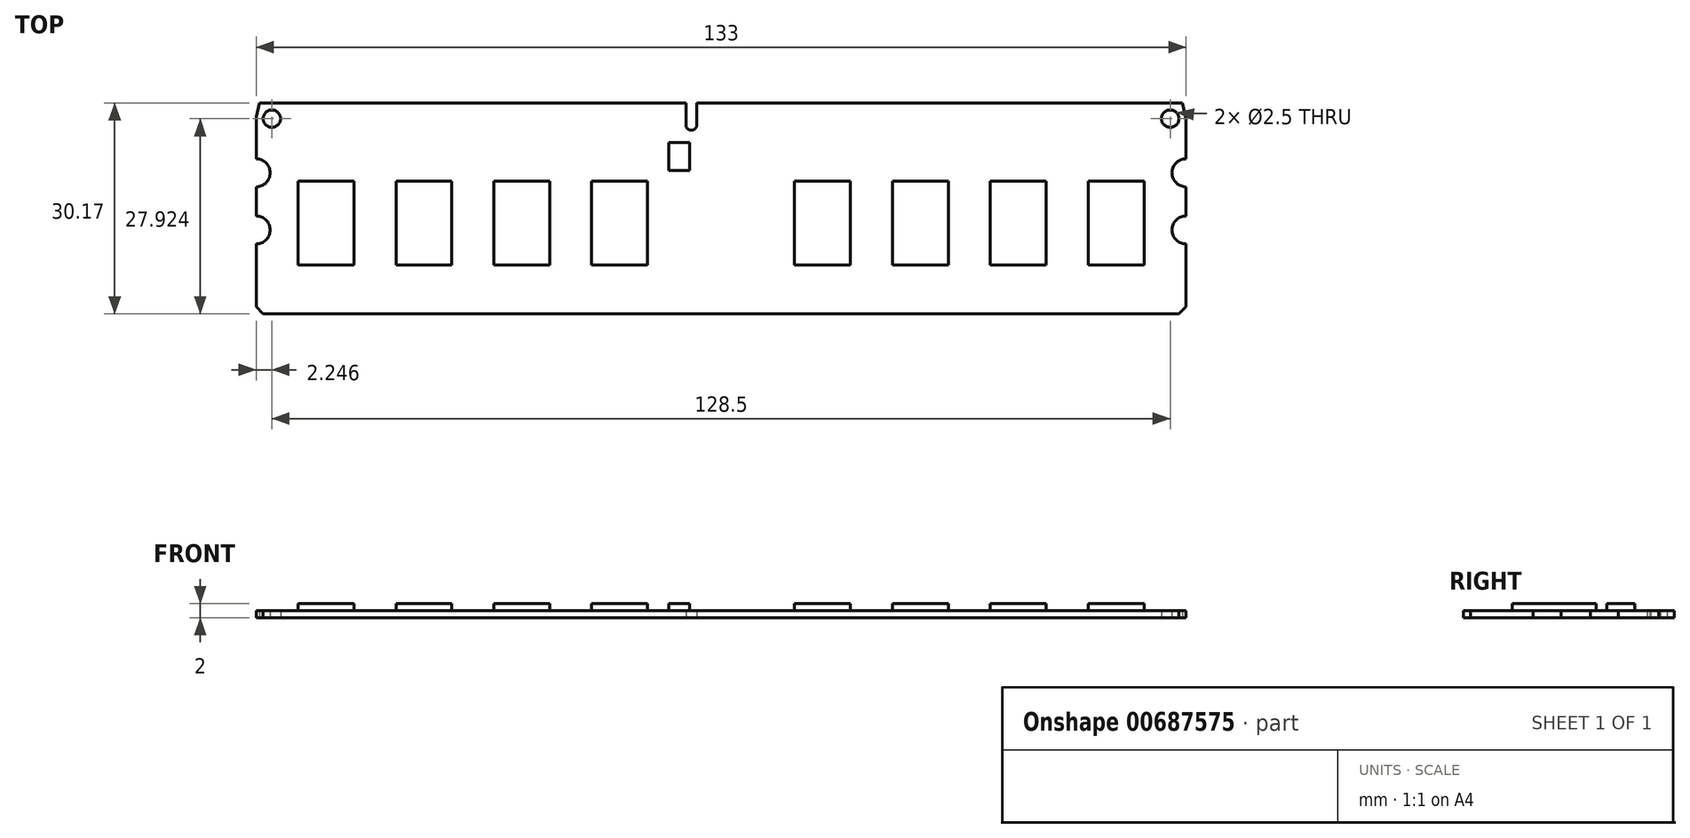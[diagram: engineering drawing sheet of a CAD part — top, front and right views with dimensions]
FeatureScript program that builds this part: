
annotation { "Feature Type Name" : "Feature", "Feature Type Description" : "" }
export const myFeature = defineFeature(function(context is Context, id is Id, definition is map)
    precondition{}
    {
        {
            var Q0;
            Q0=qCreatedBy(makeId("Top.planeOp"),FACE);
            var sketch = newSketch(context, id + "F0", { "sketchPlane" : qUnion([Q0])});
            skLineSegment(sketch, "E0.bottom", {"start": v(-59.6, 3.36) * mm, "end": v(1.4, 3.36) * mm});
            skLineSegment(sketch, "E0.top", {"start": v(-59.1, -26.81) * mm, "end": v(71.9, -26.81) * mm});
            skLineSegment(sketch, "E0.left", {"start": v(-60.1, 1.36) * mm, "end": v(-60.1, -4.64) * mm});
            skLineSegment(sketch, "E0.right", {"start": v(72.9, 1.13) * mm, "end": v(72.9, -4.64) * mm});
            skPoint(sketch, "E1.center.orphan", {"position": v(-60.1, -16.81) * mm});
            skArc(sketch, "E2", {"start": v(-60.1, -16.81) * mm, "mid": v(-58.1, -14.81) * mm, "end": v(-60.1, -12.81) * mm});
            skArc(sketch, "E3", {"start": v(-60.1, -8.64) * mm, "mid": v(-58.1, -6.64) * mm, "end": v(-60.1, -4.64) * mm});
            skLineSegment(sketch, "E4.trimOffspring", {"start": v(-60.1, -8.64) * mm, "end": v(-60.1, -12.81) * mm});
            skLineSegment(sketch, "E5.trimOffspring", {"start": v(-60.1, -16.81) * mm, "end": v(-60.1, -25.81) * mm});
            skArc(sketch, "E6", {"start": v(72.9, -4.64) * mm, "mid": v(70.9, -6.64) * mm, "end": v(72.9, -8.64) * mm});
            skArc(sketch, "E7", {"start": v(72.9, -12.81) * mm, "mid": v(70.9, -14.81) * mm, "end": v(72.9, -16.81) * mm});
            skLineSegment(sketch, "E8.trimOffspring", {"start": v(72.9, -8.64) * mm, "end": v(72.9, -12.81) * mm});
            skLineSegment(sketch, "E9.trimOffspring", {"start": v(72.9, -16.81) * mm, "end": v(72.9, -25.81) * mm});
            skLineSegment(sketch, "E10", {"start": v(-60.1, 1.36) * mm, "end": v(-59.6, 3.36) * mm});
            skLineSegment(sketch, "E11", {"start": v(72.9, 1.13) * mm, "end": v(72.4, 3.36) * mm});
            skLineSegment(sketch, "E12", {"start": v(-60.1, -25.81) * mm, "end": v(-59.1, -26.81) * mm});
            skLineSegment(sketch, "E13", {"start": v(72.9, -25.81) * mm, "end": v(71.9, -26.81) * mm});
            skLineSegment(sketch, "E14", {"start": v(72.4, 13.73) * mm, "end": v(2.9, 13.73) * mm});
            skLineSegment(sketch, "E15", {"start": v(-60.1, 13.73) * mm, "end": v(1.4, 13.73) * mm});
            skLineSegment(sketch, "E16", {"start": v(1.4, 3.36) * mm, "end": v(1.4, 0) * mm});
            skLineSegment(sketch, "E17", {"start": v(2.9, 3.36) * mm, "end": v(2.9, 0) * mm});
            skArc(sketch, "E18", {"start": v(1.4, 0) * mm, "mid": v(2.16, -0.55) * mm, "end": v(2.9, 0) * mm});
            skLineSegment(sketch, "E19.trimOffspring", {"start": v(2.9, 3.36) * mm, "end": v(72.4, 3.36) * mm});
            skCircle(sketch, "E20", {"center": v(-57.84, 1.11) * mm, "radius": 1.25 * mm});
            skCircle(sketch, "E21", {"center": v(70.66, 1.11) * mm, "radius": 1.25 * mm});
            skSolve(sketch);
        }
        {
            var Q0;
            Q0=makeQuery(id+"F0.imprint","IMPRINT",FACE,{"disambiguationData":[TD([[makeQuery(id+"F0.imprint","IMPRINT",EDGE,{"derivedFrom":sQuery(id+"F0.wireOp",EDGE,"E0.bottom")}),-1.0]])]});
            extrude(context, id + "F1", {"entities" : qUnion([Q0]), "depth" : 1 * mm, "offsetDistance" : 25 * mm});
        }
        {
            var Q0;
            Q0=makeQuery(id+"F1.opExtrude","CAP_FACE",FACE,{"disambiguationData":[OSD([sQuery(id+"F0.wireOp",EDGE,"E0.bottom"),sQuery(id+"F0.wireOp",EDGE,"E0.top"),sQuery(id+"F0.wireOp",EDGE,"E0.left"),sQuery(id+"F0.wireOp",EDGE,"E0.right"),sQuery(id+"F0.wireOp",EDGE,"E2"),sQuery(id+"F0.wireOp",EDGE,"E3"),sQuery(id+"F0.wireOp",EDGE,"E4.trimOffspring"),sQuery(id+"F0.wireOp",EDGE,"E5.trimOffspring"),sQuery(id+"F0.wireOp",EDGE,"E6"),sQuery(id+"F0.wireOp",EDGE,"E7"),sQuery(id+"F0.wireOp",EDGE,"E8.trimOffspring"),sQuery(id+"F0.wireOp",EDGE,"E9.trimOffspring"),sQuery(id+"F0.wireOp",EDGE,"E10"),sQuery(id+"F0.wireOp",EDGE,"E11"),sQuery(id+"F0.wireOp",EDGE,"E12"),sQuery(id+"F0.wireOp",EDGE,"E13"),sQuery(id+"F0.wireOp",EDGE,"E16"),sQuery(id+"F0.wireOp",EDGE,"E17"),sQuery(id+"F0.wireOp",EDGE,"E18"),sQuery(id+"F0.wireOp",EDGE,"E19.trimOffspring"),sQuery(id+"F0.wireOp",EDGE,"E20"),sQuery(id+"F0.wireOp",EDGE,"E21")])],"isStart":false});
            var sketch = newSketch(context, id + "F2", { "sketchPlane" : qUnion([Q0])});
            skLineSegment(sketch, "E22.bottom", {"start": v(-54.1, -19.81) * mm, "end": v(-46.1, -19.81) * mm});
            skLineSegment(sketch, "E22.top", {"start": v(-54.1, -7.81) * mm, "end": v(-46.1, -7.81) * mm});
            skLineSegment(sketch, "E22.left", {"start": v(-54.1, -19.81) * mm, "end": v(-54.1, -7.81) * mm});
            skLineSegment(sketch, "E22.right", {"start": v(-46.1, -19.81) * mm, "end": v(-46.1, -7.81) * mm});
            skLineSegment(sketch, "E23.bottom", {"start": v(-40.1, -19.81) * mm, "end": v(-32.1, -19.81) * mm});
            skLineSegment(sketch, "E23.top", {"start": v(-40.1, -7.81) * mm, "end": v(-32.1, -7.81) * mm});
            skLineSegment(sketch, "E23.left", {"start": v(-40.1, -19.81) * mm, "end": v(-40.1, -7.81) * mm});
            skLineSegment(sketch, "E23.right", {"start": v(-32.1, -19.81) * mm, "end": v(-32.1, -7.81) * mm});
            skLineSegment(sketch, "E24.bottom", {"start": v(-26.1, -7.81) * mm, "end": v(-18.1, -7.81) * mm});
            skLineSegment(sketch, "E24.top", {"start": v(-26.1, -19.81) * mm, "end": v(-18.1, -19.81) * mm});
            skLineSegment(sketch, "E24.left", {"start": v(-26.1, -7.81) * mm, "end": v(-26.1, -19.81) * mm});
            skLineSegment(sketch, "E24.right", {"start": v(-18.1, -7.81) * mm, "end": v(-18.1, -19.81) * mm});
            skLineSegment(sketch, "E25.bottom", {"start": v(-12.1, -7.81) * mm, "end": v(-4.1, -7.81) * mm});
            skLineSegment(sketch, "E25.top", {"start": v(-12.1, -19.81) * mm, "end": v(-4.1, -19.81) * mm});
            skLineSegment(sketch, "E25.left", {"start": v(-12.1, -7.81) * mm, "end": v(-12.1, -19.81) * mm});
            skLineSegment(sketch, "E25.right", {"start": v(-4.1, -7.81) * mm, "end": v(-4.1, -19.81) * mm});
            skLineSegment(sketch, "E26.bottom", {"start": v(66.9, -7.81) * mm, "end": v(58.9, -7.81) * mm});
            skLineSegment(sketch, "E26.top", {"start": v(66.9, -19.81) * mm, "end": v(58.9, -19.81) * mm});
            skLineSegment(sketch, "E26.left", {"start": v(66.9, -7.81) * mm, "end": v(66.9, -19.81) * mm});
            skLineSegment(sketch, "E26.right", {"start": v(58.9, -7.81) * mm, "end": v(58.9, -19.81) * mm});
            skLineSegment(sketch, "E27.bottom", {"start": v(52.9, -7.81) * mm, "end": v(44.9, -7.81) * mm});
            skLineSegment(sketch, "E27.top", {"start": v(52.9, -19.81) * mm, "end": v(44.9, -19.81) * mm});
            skLineSegment(sketch, "E27.left", {"start": v(52.9, -7.81) * mm, "end": v(52.9, -19.81) * mm});
            skLineSegment(sketch, "E27.right", {"start": v(44.9, -7.81) * mm, "end": v(44.9, -19.81) * mm});
            skLineSegment(sketch, "E28.bottom", {"start": v(38.9, -7.81) * mm, "end": v(30.9, -7.81) * mm});
            skLineSegment(sketch, "E28.top", {"start": v(38.9, -19.81) * mm, "end": v(30.9, -19.81) * mm});
            skLineSegment(sketch, "E28.left", {"start": v(38.9, -7.81) * mm, "end": v(38.9, -19.81) * mm});
            skLineSegment(sketch, "E28.right", {"start": v(30.9, -7.81) * mm, "end": v(30.9, -19.81) * mm});
            skLineSegment(sketch, "E29.bottom", {"start": v(24.9, -7.81) * mm, "end": v(16.9, -7.81) * mm});
            skLineSegment(sketch, "E29.top", {"start": v(24.9, -19.81) * mm, "end": v(16.9, -19.81) * mm});
            skLineSegment(sketch, "E29.left", {"start": v(24.9, -7.81) * mm, "end": v(24.9, -19.81) * mm});
            skLineSegment(sketch, "E29.right", {"start": v(16.9, -7.81) * mm, "end": v(16.9, -19.81) * mm});
            skLineSegment(sketch, "E30.bottom", {"start": v(-1.1, -6.31) * mm, "end": v(1.9, -6.31) * mm});
            skLineSegment(sketch, "E30.top", {"start": v(-1.1, -2.31) * mm, "end": v(1.9, -2.31) * mm});
            skLineSegment(sketch, "E30.left", {"start": v(-1.1, -6.31) * mm, "end": v(-1.1, -2.31) * mm});
            skLineSegment(sketch, "E30.right", {"start": v(1.9, -6.31) * mm, "end": v(1.9, -2.31) * mm});
            skPoint(sketch, "E31.endSnap0", {"position": v(6.4, -26.81) * mm});
            skSolve(sketch);
        }
        {
            var Q0;
            Q0 = qSketchRegion(id + "F2", true);
            extrude(context, id + "F3", {"entities" : qUnion([Q0]), "operationType" : NewBodyOperationType.ADD, "depth" : 1 * mm, "offsetDistance" : 25 * mm});
        }
    });
